# Revit family: 53-30-005-DN32-50
name_source: partatom
category: Pipe Accessories
units: mm (PartAtom-declared; Revit-internal decimal feet)

## family parameters
Always vertical = Yes
Cut with Voids When Loaded = No
Part Type = Valve - Breaks Into
Round Connector Dimension = Use Diameter
Shared = No
Work Plane-Based = No

## types (3) — shared parameters
Body_Wall_thickness = 10 mm  [stored 0.0328084 ft]
Circle_cut = 2 mm  [stored 0.00656168 ft]
DN = 50 mm  [stored 0.164042 ft]
DN32_PN10 = 53-032-30-9007
DN40_PN10 = 53-040-30-9007
DN50_PN10 = 53-050-30-9007
Description_ = AVK BALL CHECK VALVE, MJ/THREAD
Ear_Height = 5 mm  [stored 0.0164042 ft]
Ear_Reference_2 = 3 mm  [stored 0.00984252 ft]
Ear_width = 5 mm  [stored 0.0164042 ft]
Fillet_Thickness_2 = 3 mm  [stored 0.00984252 ft]
Flange_Thickness = 19 mm  [stored 0.062336 ft]
Hook_Distance = 10 mm  [stored 0.0328084 ft]
Hook_Distance_2 = 2 mm  [stored 0.00656168 ft]
Hook_Height = 10 mm  [stored 0.0328084 ft]
Hook_Height_2 = 5 mm  [stored 0.0164042 ft]
Hook_Legnth = 5 mm  [stored 0.0164042 ft]
RF_Thickness = 3 mm  [stored 0.00984252 ft]
Rib_Distance = 10 mm  [stored 0.0328084 ft]
Rib_Distance_2 = 10 mm  [stored 0.0328084 ft]
Search_table = 53-30-005-DN32-50
URL product pages = https://www.avkvalves.com

## per-type parameters (varying)
- DN050: Body_Height_1=33 mm  [stored 0.108268 ft]; Body_Height_2=77 mm  [stored 0.252625 ft]; Body_Height_3=35 mm  [stored 0.114829 ft]; Body_Ref=71 mm  [stored 0.23294 ft]; Body_distance_1=10 mm  [stored 0.0328084 ft]; Body_distance_3=20 mm  [stored 0.0656168 ft]; Bottom_height=5 mm  [stored 0.0164042 ft]; Chamfer=20 mm  [stored 0.0656168 ft]; Chamfer_Ref=43 mm  [stored 0.141076 ft]; Circle_Height=15 mm  [stored 0.0492126 ft]; Circle_Height_2=10 mm  [stored 0.0328084 ft]; Circle_Length=30 mm  [stored 0.0984252 ft]; Circle_Radius_2=475 mm; Circle_radius=40 mm  [stored 0.131234 ft]; Cut_Height_Ref=67.33 mm; Cut_ref=35 mm  [stored 0.114829 ft]; DN_ref=70 mm  [stored 0.229659 ft]; Distance_1=14 mm  [stored 0.0459318 ft]; Distance_2=51 mm  [stored 0.167323 ft]; Distance_3=67 mm  [stored 0.219816 ft]; Distance_4=2 mm  [stored 0.00656168 ft]; Ear_Lenght_2=31 mm  [stored 0.101706 ft]; Ear_Length=62 mm  [stored 0.203412 ft]; Ear_Reference=73 mm  [stored 0.239501 ft]; F_OD=82.5 mm; Flange_Dia=43 mm  [stored 0.141076 ft]; Flange_Thickness_2=5 mm  [stored 0.0164042 ft]; H=101 mm; H3=144 mm; H3_ref=43 mm  [stored 0.141076 ft]; ID=25 mm  [stored 0.082021 ft]; L=180 mm; L2=270 mm; Nominal_Diameter=50 mm  [stored 0.164042 ft]; RF=49 mm  [stored 0.160761 ft]; Rib_height=20 mm  [stored 0.0656168 ft]
- DN040: Body_Height_1=30 mm  [stored 0.0984252 ft]; Body_Height_2=55 mm  [stored 0.180446 ft]; Body_Height_3=29 mm  [stored 0.0951444 ft]; Body_Ref=51 mm  [stored 0.167323 ft]; Body_distance_1=8 mm  [stored 0.0262467 ft]; Body_distance_3=15 mm  [stored 0.0492126 ft]; Bottom_height=3 mm  [stored 0.00984252 ft]; Chamfer=15 mm  [stored 0.0492126 ft]; Chamfer_Ref=35.5 mm  [stored 0.11647 ft]; Circle_Height=10 mm  [stored 0.0328084 ft]; Circle_Height_2=8 mm  [stored 0.0262467 ft]; Circle_Length=20 mm  [stored 0.0656168 ft]; Circle_Radius_2=320 mm; Circle_radius=30 mm  [stored 0.0984252 ft]; Cut_Height_Ref=55.33 mm; Cut_ref=30 mm  [stored 0.0984252 ft]; DN_ref=60 mm  [stored 0.19685 ft]; Distance_1=10 mm  [stored 0.0328084 ft]; Distance_2=40 mm  [stored 0.131234 ft]; Distance_3=55 mm  [stored 0.180446 ft]; Distance_4=5 mm  [stored 0.0164042 ft]; Ear_Lenght_2=26.75 mm  [stored 0.0877625 ft]; Ear_Length=53.5 mm  [stored 0.175525 ft]; Ear_Reference=65 mm  [stored 0.213255 ft]; F_OD=77.5 mm; Flange_Dia=31 mm  [stored 0.101706 ft]; Flange_Thickness_2=4 mm  [stored 0.0131234 ft]; H=83 mm; H3=118 mm; H3_ref=35 mm  [stored 0.114829 ft]; ID=20 mm  [stored 0.0656168 ft]; L=140 mm; L2=210 mm; Nominal_Diameter=40 mm  [stored 0.131234 ft]; RF=44 mm  [stored 0.144357 ft]; Rib_height=15 mm  [stored 0.0492126 ft]
- DN032: Body_Height_1=26 mm; Body_Height_2=55 mm  [stored 0.180446 ft]; Body_Height_3=29 mm  [stored 0.0951444 ft]; Body_Ref=51 mm  [stored 0.167323 ft]; Body_distance_1=8 mm  [stored 0.0262467 ft]; Body_distance_3=15 mm  [stored 0.0492126 ft]; Bottom_height=3 mm  [stored 0.00984252 ft]; Chamfer=15 mm  [stored 0.0492126 ft]; Chamfer_Ref=35.5 mm  [stored 0.11647 ft]; Circle_Height=10 mm  [stored 0.0328084 ft]; Circle_Height_2=8 mm  [stored 0.0262467 ft]; Circle_Length=20 mm  [stored 0.0656168 ft]; Circle_Radius_2=320 mm; Circle_radius=30 mm  [stored 0.0984252 ft]; Cut_Height_Ref=55.33 mm; Cut_ref=26 mm; DN_ref=52 mm  [stored 0.170604 ft]; Distance_1=10 mm  [stored 0.0328084 ft]; Distance_2=40 mm  [stored 0.131234 ft]; Distance_3=55 mm  [stored 0.180446 ft]; Distance_4=5 mm  [stored 0.0164042 ft]; Ear_Lenght_2=26.75 mm  [stored 0.0877625 ft]; Ear_Length=53.5 mm  [stored 0.175525 ft]; Ear_Reference=65 mm  [stored 0.213255 ft]; F_OD=77.5 mm; Flange_Dia=31 mm  [stored 0.101706 ft]; Flange_Thickness_2=4 mm  [stored 0.0131234 ft]; H=83 mm; H3=118 mm; H3_ref=35 mm  [stored 0.114829 ft]; ID=16 mm  [stored 0.0524934 ft]; L=140 mm; L2=210 mm; Nominal_Diameter=32 mm  [stored 0.104987 ft]; RF=44 mm  [stored 0.144357 ft]; Rib_height=15 mm  [stored 0.0492126 ft]

note: [stored X ft] marks values corroborated as IEEE doubles in the binary element streams (Revit-internal decimal feet)

## geometry (parser evidence)
native form markers: Sweep x11
no freeform markers — native parametric forms only
